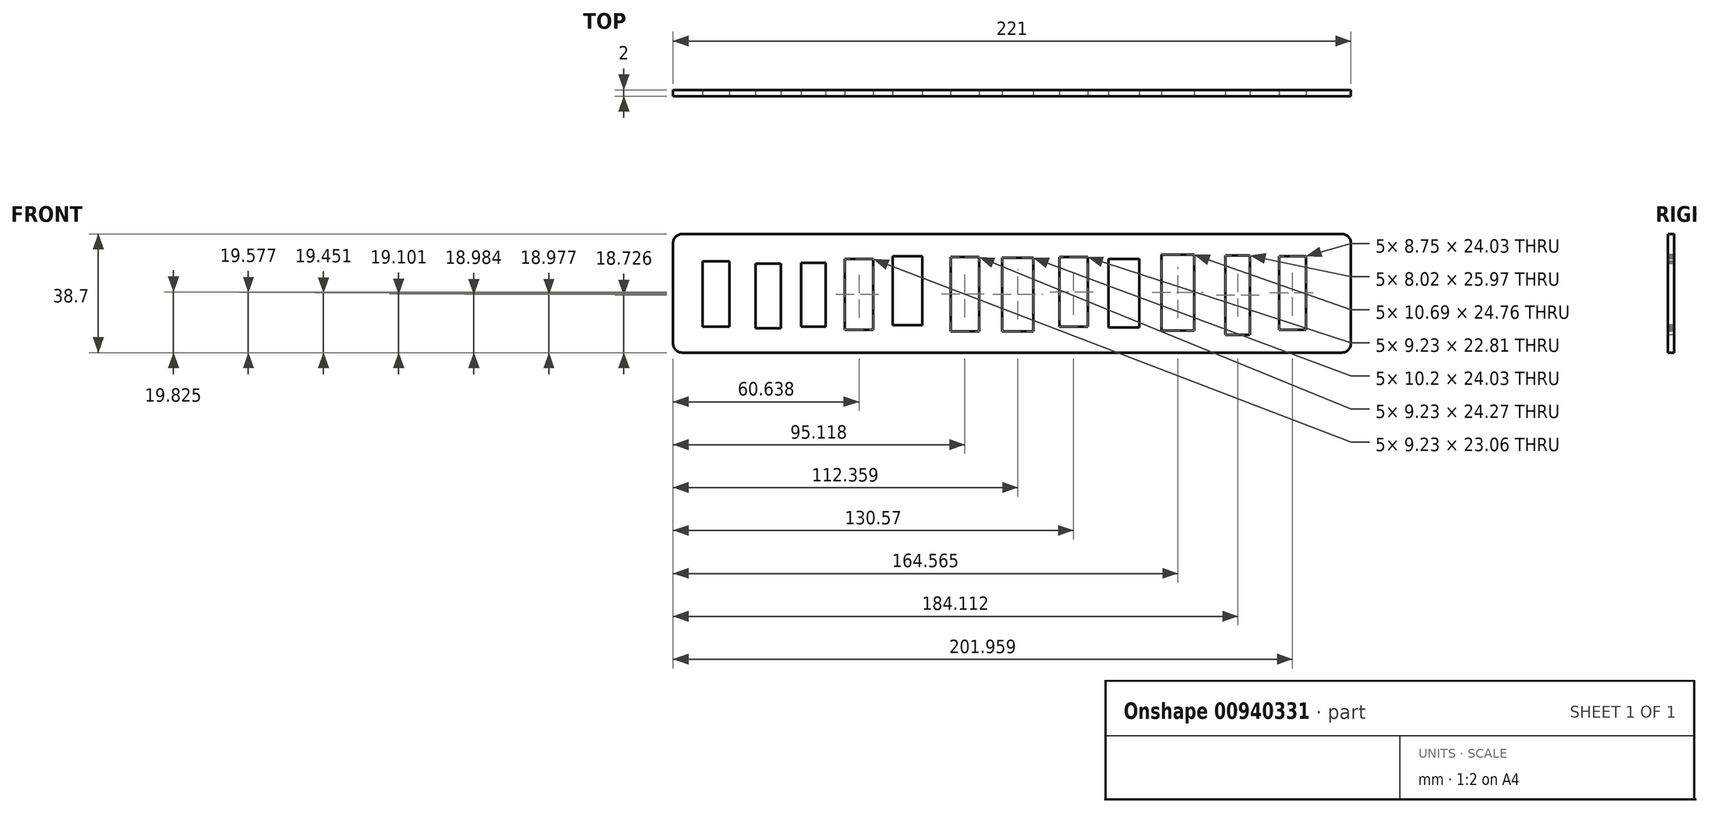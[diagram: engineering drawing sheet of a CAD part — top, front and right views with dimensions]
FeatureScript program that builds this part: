
annotation { "Feature Type Name" : "Feature", "Feature Type Description" : "" }
export const myFeature = defineFeature(function(context is Context, id is Id, definition is map)
    precondition{}
    {
        {
            var Q0;
            Q0=qCreatedBy(makeId("Front.planeOp"),FACE);
            var sketch = newSketch(context, id + "F0", { "sketchPlane" : qUnion([Q0])});
            skLineSegment(sketch, "E0.bottom", {"start": v(110.5, -19.35) * mm, "end": v(-110.5, -19.35) * mm});
            skLineSegment(sketch, "E0.top", {"start": v(110.5, 19.35) * mm, "end": v(-110.5, 19.35) * mm});
            skLineSegment(sketch, "E0.left", {"start": v(110.5, -19.35) * mm, "end": v(110.5, 19.35) * mm});
            skLineSegment(sketch, "E0.right", {"start": v(-110.5, -19.35) * mm, "end": v(-110.5, 19.35) * mm});
            skPoint(sketch, "E0.middle", {"position": v(0, 0) * mm});
            skLineSegment(sketch, "E1.bottom", {"start": v(-83.62, 9.71) * mm, "end": v(-75.36, 9.71) * mm});
            skLineSegment(sketch, "E1.top", {"start": v(-83.62, -11.4) * mm, "end": v(-75.36, -11.4) * mm});
            skLineSegment(sketch, "E1.left", {"start": v(-83.62, 9.71) * mm, "end": v(-83.62, -11.4) * mm});
            skLineSegment(sketch, "E1.right", {"start": v(-75.36, 9.71) * mm, "end": v(-75.36, -11.4) * mm});
            skLineSegment(sketch, "E2.bottom", {"start": v(-68.8, 9.95) * mm, "end": v(-60.79, 9.95) * mm});
            skLineSegment(sketch, "E2.top", {"start": v(-68.8, -10.92) * mm, "end": v(-60.79, -10.92) * mm});
            skLineSegment(sketch, "E2.left", {"start": v(-68.8, 9.95) * mm, "end": v(-68.8, -10.92) * mm});
            skLineSegment(sketch, "E2.right", {"start": v(-60.79, 9.95) * mm, "end": v(-60.79, -10.92) * mm});
            skLineSegment(sketch, "E3.bottom", {"start": v(-54.48, 11.16) * mm, "end": v(-45.25, 11.16) * mm});
            skLineSegment(sketch, "E3.top", {"start": v(-54.48, -11.9) * mm, "end": v(-45.25, -11.9) * mm});
            skLineSegment(sketch, "E3.left", {"start": v(-54.48, 11.16) * mm, "end": v(-54.48, -11.9) * mm});
            skLineSegment(sketch, "E3.right", {"start": v(-45.25, 11.16) * mm, "end": v(-45.25, -11.9) * mm});
            skLineSegment(sketch, "E4.bottom", {"start": v(-38.94, 12.13) * mm, "end": v(-29.22, 12.13) * mm});
            skLineSegment(sketch, "E4.top", {"start": v(-38.94, -10.44) * mm, "end": v(-29.22, -10.44) * mm});
            skLineSegment(sketch, "E4.left", {"start": v(-38.94, 12.13) * mm, "end": v(-38.94, -10.44) * mm});
            skLineSegment(sketch, "E4.right", {"start": v(-29.22, 12.13) * mm, "end": v(-29.22, -10.44) * mm});
            skLineSegment(sketch, "E5.bottom", {"start": v(-20, 11.89) * mm, "end": v(-10.76, 11.89) * mm});
            skLineSegment(sketch, "E5.top", {"start": v(-20, -12.38) * mm, "end": v(-10.76, -12.38) * mm});
            skLineSegment(sketch, "E5.left", {"start": v(-20, 11.89) * mm, "end": v(-20, -12.38) * mm});
            skLineSegment(sketch, "E5.right", {"start": v(-10.76, 11.89) * mm, "end": v(-10.76, -12.38) * mm});
            skLineSegment(sketch, "E6.bottom", {"start": v(-3.24, 11.64) * mm, "end": v(6.96, 11.64) * mm});
            skLineSegment(sketch, "E6.top", {"start": v(-3.24, -12.39) * mm, "end": v(6.96, -12.39) * mm});
            skLineSegment(sketch, "E6.left", {"start": v(-3.24, 11.64) * mm, "end": v(-3.24, -12.39) * mm});
            skLineSegment(sketch, "E6.right", {"start": v(6.96, 11.64) * mm, "end": v(6.96, -12.39) * mm});
            skLineSegment(sketch, "E7.bottom", {"start": v(15.45, 11.88) * mm, "end": v(24.69, 11.88) * mm});
            skLineSegment(sketch, "E7.top", {"start": v(15.45, -10.93) * mm, "end": v(24.69, -10.93) * mm});
            skLineSegment(sketch, "E7.left", {"start": v(15.45, 11.88) * mm, "end": v(15.45, -10.93) * mm});
            skLineSegment(sketch, "E7.right", {"start": v(24.69, 11.88) * mm, "end": v(24.69, -10.93) * mm});
            skLineSegment(sketch, "E8.bottom", {"start": v(31.48, 11.15) * mm, "end": v(41.44, 11.15) * mm});
            skLineSegment(sketch, "E8.top", {"start": v(31.48, -11.18) * mm, "end": v(41.44, -11.18) * mm});
            skLineSegment(sketch, "E8.left", {"start": v(31.48, 11.15) * mm, "end": v(31.48, -11.18) * mm});
            skLineSegment(sketch, "E8.right", {"start": v(41.44, 11.15) * mm, "end": v(41.44, -11.18) * mm});
            skLineSegment(sketch, "E9.bottom", {"start": v(48.72, 12.6) * mm, "end": v(59.41, 12.6) * mm});
            skLineSegment(sketch, "E9.top", {"start": v(48.72, -12.15) * mm, "end": v(59.41, -12.15) * mm});
            skLineSegment(sketch, "E9.left", {"start": v(48.72, 12.6) * mm, "end": v(48.72, -12.15) * mm});
            skLineSegment(sketch, "E9.right", {"start": v(59.41, 12.6) * mm, "end": v(59.41, -12.15) * mm});
            skLineSegment(sketch, "E10.bottom", {"start": v(69.6, 12.36) * mm, "end": v(77.62, 12.36) * mm});
            skLineSegment(sketch, "E10.top", {"start": v(69.6, -13.6) * mm, "end": v(77.62, -13.6) * mm});
            skLineSegment(sketch, "E10.left", {"start": v(69.6, 12.36) * mm, "end": v(69.6, -13.6) * mm});
            skLineSegment(sketch, "E10.right", {"start": v(77.62, 12.36) * mm, "end": v(77.62, -13.6) * mm});
            skLineSegment(sketch, "E11.bottom", {"start": v(87.09, 12.12) * mm, "end": v(95.83, 12.12) * mm});
            skLineSegment(sketch, "E11.top", {"start": v(87.09, -11.91) * mm, "end": v(95.83, -11.91) * mm});
            skLineSegment(sketch, "E11.left", {"start": v(87.09, 12.12) * mm, "end": v(87.09, -11.91) * mm});
            skLineSegment(sketch, "E11.right", {"start": v(95.83, 12.12) * mm, "end": v(95.83, -11.91) * mm});
            skLineSegment(sketch, "E12.bottom", {"start": v(-100.83, 10.44) * mm, "end": v(-92.1, 10.44) * mm});
            skLineSegment(sketch, "E12.top", {"start": v(-100.83, -10.92) * mm, "end": v(-92.1, -10.92) * mm});
            skLineSegment(sketch, "E12.left", {"start": v(-100.83, 10.44) * mm, "end": v(-100.83, -10.92) * mm});
            skLineSegment(sketch, "E12.right", {"start": v(-92.1, 10.44) * mm, "end": v(-92.1, -10.92) * mm});
            skSolve(sketch);
        }
        {
            var Q0;
            Q0=makeQuery(id+"F0.imprint","IMPRINT",FACE,{"disambiguationData":[TD([[makeQuery(id+"F0.imprint","IMPRINT",EDGE,{"derivedFrom":sQuery(id+"F0.wireOp",EDGE,"E0.bottom")}),-1.0]])]});
            extrude(context, id + "F1", {"entities" : qUnion([Q0]), "oppositeDirection" : true, "depth" : 2 * mm, "offsetDistance" : 25 * mm});
        }
        {
            var Q0;
            Q0=makeQuery(id+"F1.opExtrude","SWEPT_EDGE",EDGE,{"disambiguationData":[OSD([sQuery(id+"F0.wireOp",EDGE,"E0.top"),sQuery(id+"F0.wireOp",EDGE,"E0.right")])]});
            var Q1;
            Q1=makeQuery(id+"F1.opExtrude","SWEPT_EDGE",EDGE,{"disambiguationData":[OSD([sQuery(id+"F0.wireOp",EDGE,"E0.top"),sQuery(id+"F0.wireOp",EDGE,"E0.left")])]});
            var Q2;
            Q2=makeQuery(id+"F1.opExtrude","SWEPT_EDGE",EDGE,{"disambiguationData":[OSD([sQuery(id+"F0.wireOp",EDGE,"E0.bottom"),sQuery(id+"F0.wireOp",EDGE,"E0.left")])]});
            var Q3;
            Q3=makeQuery(id+"F1.opExtrude","SWEPT_EDGE",EDGE,{"disambiguationData":[OSD([sQuery(id+"F0.wireOp",EDGE,"E0.bottom"),sQuery(id+"F0.wireOp",EDGE,"E0.right")])]});
            fillet(context, id + "F2", {"entities" : qUnion([Q0, Q1, Q2, Q3]), "radius" : 3 * mm, "tangentPropagation" : true, "allowEdgeOverflow" : false});
        }
    });
